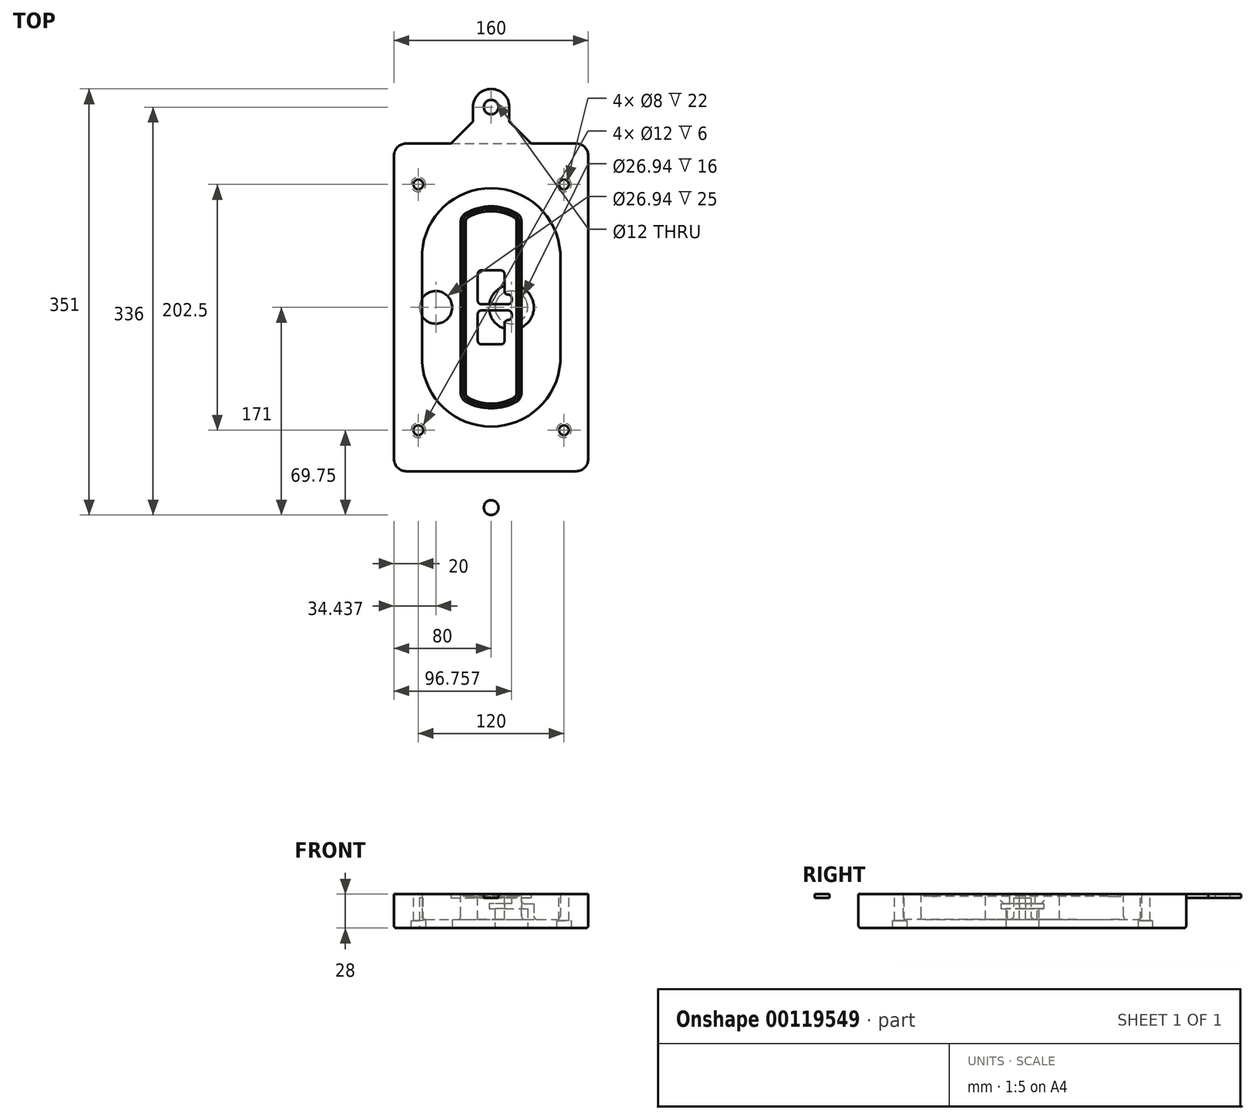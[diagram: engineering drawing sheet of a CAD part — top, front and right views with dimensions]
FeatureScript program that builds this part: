
annotation { "Feature Type Name" : "Feature", "Feature Type Description" : "" }
export const myFeature = defineFeature(function(context is Context, id is Id, definition is map)
    precondition{}
    {
        {
            var Q0;
            Q0=qCreatedBy(makeId("Top.planeOp"),FACE);
            var sketch = newSketch(context, id + "F0", { "sketchPlane" : qUnion([Q0])});
            skPoint(sketch, "E0.rect.middle", {"position": v(0, 0) * mm});
            skLineSegment(sketch, "E1.bottom", {"start": v(-70, -135) * mm, "end": v(70, -135) * mm});
            skLineSegment(sketch, "E1.top", {"start": v(-70, 135) * mm, "end": v(70, 135) * mm});
            skLineSegment(sketch, "E1.left", {"start": v(-80, -125) * mm, "end": v(-80, 125) * mm});
            skLineSegment(sketch, "E1.right", {"start": v(80, -125) * mm, "end": v(80, 125) * mm});
            skLineSegment(sketch, "E2", {"start": v(-80, 135) * mm, "end": v(80, -135) * mm, "construction": true});
            skLineSegment(sketch, "E3", {"start": v(80, 135) * mm, "end": v(-80, -135) * mm, "construction": true});
            skCircle(sketch, "E4", {"center": v(-60, 101.25) * mm, "radius": 4 * mm});
            skCircle(sketch, "E5", {"center": v(60, 101.25) * mm, "radius": 4 * mm});
            skCircle(sketch, "E6", {"center": v(60, -101.25) * mm, "radius": 4 * mm});
            skCircle(sketch, "E7", {"center": v(-60, -101.25) * mm, "radius": 4 * mm});
            skLineSegment(sketch, "E8", {"start": v(-60, 101.25) * mm, "end": v(60, 101.25) * mm, "construction": true});
            skLineSegment(sketch, "E9", {"start": v(60, 101.25) * mm, "end": v(60, -101.25) * mm, "construction": true});
            skLineSegment(sketch, "E10", {"start": v(60, -101.25) * mm, "end": v(-60, -101.25) * mm, "construction": true});
            skLineSegment(sketch, "E11", {"start": v(-60, -101.25) * mm, "end": v(-60, 101.25) * mm, "construction": true});
            skLineSegment(sketch, "E12", {"start": v(-60, 44.66) * mm, "end": v(-60, -44.66) * mm});
            skLineSegment(sketch, "E13", {"start": v(60, 44.66) * mm, "end": v(60, -44.66) * mm});
            skArc(sketch, "E14", {"start": v(59.98, 45.37) * mm, "mid": v(0, 101.25) * mm, "end": v(-59.98, 45.37) * mm});
            skArc(sketch, "E15", {"start": v(-59.98, -45.37) * mm, "mid": v(0, -101.25) * mm, "end": v(59.98, -45.37) * mm});
            skLineSegment(sketch, "E16", {"start": v(-60, 0) * mm, "end": v(60, 0) * mm, "construction": true});
            skPoint(sketch, "E17.visualSharp", {"position": v(-60, -45) * mm});
            skArc(sketch, "E17.filletArc", {"start": v(-60, -44.66) * mm, "mid": v(-60, -45.02) * mm, "end": v(-59.98, -45.37) * mm});
            skPoint(sketch, "E18.visualSharp", {"position": v(-60, 45) * mm});
            skArc(sketch, "E18.filletArc", {"start": v(-59.98, 45.37) * mm, "mid": v(-60, 45.02) * mm, "end": v(-60, 44.66) * mm});
            skPoint(sketch, "E19.visualSharp", {"position": v(60, 45) * mm});
            skArc(sketch, "E19.filletArc", {"start": v(60, 44.66) * mm, "mid": v(60, 45.02) * mm, "end": v(59.98, 45.37) * mm});
            skPoint(sketch, "E20.visualSharp", {"position": v(60, -45) * mm});
            skArc(sketch, "E20.filletArc", {"start": v(59.98, -45.37) * mm, "mid": v(60, -45.02) * mm, "end": v(60, -44.66) * mm});
            skPoint(sketch, "E21.visualSharp", {"position": v(-80, 135) * mm});
            skArc(sketch, "E21.filletArc", {"start": v(-70, 135) * mm, "mid": v(-77.07, 132.07) * mm, "end": v(-80, 125) * mm});
            skPoint(sketch, "E22.visualSharp", {"position": v(80, 135) * mm});
            skArc(sketch, "E22.filletArc", {"start": v(80, 125) * mm, "mid": v(77.07, 132.07) * mm, "end": v(70, 135) * mm});
            skPoint(sketch, "E23.visualSharp", {"position": v(80, -135) * mm});
            skArc(sketch, "E23.filletArc", {"start": v(70, -135) * mm, "mid": v(77.07, -132.07) * mm, "end": v(80, -125) * mm});
            skPoint(sketch, "E24.visualSharp", {"position": v(-80, -135) * mm});
            skArc(sketch, "E24.filletArc", {"start": v(-80, -125) * mm, "mid": v(-77.07, -132.07) * mm, "end": v(-70, -135) * mm});
            skArc(sketch, "E25.0", {"start": v(57, 44.66) * mm, "mid": v(57, 44.9) * mm, "end": v(56.98, 45.16) * mm});
            skLineSegment(sketch, "E25.1", {"start": v(57, 44.66) * mm, "end": v(57, -44.66) * mm});
            skArc(sketch, "E25.2", {"start": v(56.98, -45.16) * mm, "mid": v(57, -44.9) * mm, "end": v(57, -44.66) * mm});
            skArc(sketch, "E25.3", {"start": v(-56.98, -45.16) * mm, "mid": v(0, -98.25) * mm, "end": v(56.98, -45.16) * mm});
            skArc(sketch, "E25.4", {"start": v(-57, -44.66) * mm, "mid": v(-57, -44.9) * mm, "end": v(-56.98, -45.16) * mm});
            skArc(sketch, "E25.5", {"start": v(56.98, 45.16) * mm, "mid": v(0, 98.25) * mm, "end": v(-56.98, 45.16) * mm});
            skLineSegment(sketch, "E25.6", {"start": v(-57, 44.66) * mm, "end": v(-57, -44.66) * mm});
            skArc(sketch, "E25.7", {"start": v(-56.98, 45.16) * mm, "mid": v(-57, 44.9) * mm, "end": v(-57, 44.66) * mm});
            skArc(sketch, "E26.0", {"start": v(-63.97, 45.65) * mm, "mid": v(-64, 45.16) * mm, "end": v(-64, 44.66) * mm});
            skArc(sketch, "E26.1", {"start": v(63.97, 45.65) * mm, "mid": v(0, 105.25) * mm, "end": v(-63.97, 45.65) * mm});
            skArc(sketch, "E26.2", {"start": v(64, 44.66) * mm, "mid": v(64, 45.16) * mm, "end": v(63.97, 45.65) * mm});
            skLineSegment(sketch, "E26.3", {"start": v(64, 44.66) * mm, "end": v(64, -44.66) * mm});
            skArc(sketch, "E26.4", {"start": v(63.97, -45.65) * mm, "mid": v(64, -45.16) * mm, "end": v(64, -44.66) * mm});
            skLineSegment(sketch, "E26.5", {"start": v(-64, 44.66) * mm, "end": v(-64, -44.66) * mm});
            skArc(sketch, "E26.6", {"start": v(-63.97, -45.65) * mm, "mid": v(0, -105.25) * mm, "end": v(63.97, -45.65) * mm});
            skArc(sketch, "E26.7", {"start": v(-64, -44.66) * mm, "mid": v(-64, -45.16) * mm, "end": v(-63.97, -45.65) * mm});
            skSolve(sketch);
        }
        {
            var Q0;
            Q0=makeQuery(id+"F0.imprint","IMPRINT",FACE,{"disambiguationData":[TD([[makeQuery(id+"F0.imprint","IMPRINT",EDGE,{"derivedFrom":sQuery(id+"F0.wireOp",EDGE,"E1.bottom")}),1.0]])]});
            var Q1;
            Q1=makeQuery(id+"F0.imprint","IMPRINT",FACE,{"disambiguationData":[TD([[makeQuery(id+"F0.imprint","IMPRINT",EDGE,{"derivedFrom":sQuery(id+"F0.wireOp",EDGE,"E12")}),1.0]])]});
            var Q2;
            Q2=makeQuery(id+"F0.imprint","IMPRINT",FACE,{"disambiguationData":[TD([[makeQuery(id+"F0.imprint","IMPRINT",EDGE,{"derivedFrom":sQuery(id+"F0.wireOp",EDGE,"E25.0")}),1.0]])]});
            var Q3;
            Q3=makeQuery(id+"F0.imprint","IMPRINT",FACE,{"disambiguationData":[TD([[makeQuery(id+"F0.imprint","IMPRINT",EDGE,{"derivedFrom":sQuery(id+"F0.wireOp",EDGE,"E12")}),-1.0]])]});
            extrude(context, id + "F1", {"entities" : qUnion([Q0, Q1, Q2, Q3]), "oppositeDirection" : true, "depth" : 25 * mm});
        }
        {
            var Q0;
            Q0=makeQuery(id+"F0.imprint","IMPRINT",FACE,{"disambiguationData":[TD([[makeQuery(id+"F0.imprint","IMPRINT",EDGE,{"derivedFrom":sQuery(id+"F0.wireOp",EDGE,"E12")}),1.0]])]});
            extrude(context, id + "F2", {"entities" : qUnion([Q0]), "operationType" : NewBodyOperationType.ADD, "depth" : 3 * mm});
        }
        {
            var Q0;
            Q0=makeQuery(id+"F0.imprint","IMPRINT",FACE,{"disambiguationData":[TD([[makeQuery(id+"F0.imprint","IMPRINT",EDGE,{"derivedFrom":sQuery(id+"F0.wireOp",EDGE,"E25.0")}),1.0]])]});
            extrude(context, id + "F3", {"entities" : qUnion([Q0]), "operationType" : NewBodyOperationType.REMOVE, "oppositeDirection" : true, "depth" : 18 * mm});
        }
        {
            var Q0;
            Q0=makeQuery(id+"F2.opExtrude","CAP_FACE",FACE,{"disambiguationData":[OSD([sQuery(id+"F0.wireOp",EDGE,"E12"),sQuery(id+"F0.wireOp",EDGE,"E13"),sQuery(id+"F0.wireOp",EDGE,"E14"),sQuery(id+"F0.wireOp",EDGE,"E15"),sQuery(id+"F0.wireOp",EDGE,"E17.filletArc"),sQuery(id+"F0.wireOp",EDGE,"E18.filletArc"),sQuery(id+"F0.wireOp",EDGE,"E19.filletArc"),sQuery(id+"F0.wireOp",EDGE,"E20.filletArc"),sQuery(id+"F0.wireOp",EDGE,"E25.0"),sQuery(id+"F0.wireOp",EDGE,"E25.1"),sQuery(id+"F0.wireOp",EDGE,"E25.2"),sQuery(id+"F0.wireOp",EDGE,"E25.3"),sQuery(id+"F0.wireOp",EDGE,"E25.4"),sQuery(id+"F0.wireOp",EDGE,"E25.5"),sQuery(id+"F0.wireOp",EDGE,"E25.6"),sQuery(id+"F0.wireOp",EDGE,"E25.7")])],"isStart":false});
            var sketch = newSketch(context, id + "F4", { "sketchPlane" : qUnion([Q0])});
            skArc(sketch, "E27.0", {"start": v(-20.99, -77.65) * mm, "mid": v(0, -83.25) * mm, "end": v(20.99, -77.65) * mm});
            skArc(sketch, "E28.0", {"start": v(20.99, 77.65) * mm, "mid": v(0, 83.25) * mm, "end": v(-20.99, 77.65) * mm});
            skLineSegment(sketch, "E29", {"start": v(-25, 70.71) * mm, "end": v(-25, -70.71) * mm});
            skLineSegment(sketch, "E30", {"start": v(25, 70.71) * mm, "end": v(25, -70.71) * mm});
            skLineSegment(sketch, "E31", {"start": v(-25, 75.03) * mm, "end": v(25, 75.03) * mm, "construction": true});
            skLineSegment(sketch, "E32", {"start": v(-25, -75.03) * mm, "end": v(25, -75.03) * mm, "construction": true});
            skPoint(sketch, "E33.visualSharp", {"position": v(-25, 75.03) * mm});
            skArc(sketch, "E33.filletArc", {"start": v(-20.99, 77.65) * mm, "mid": v(-23.92, 74.72) * mm, "end": v(-25, 70.71) * mm});
            skPoint(sketch, "E34.visualSharp", {"position": v(25, 75.03) * mm});
            skArc(sketch, "E34.filletArc", {"start": v(25, 70.71) * mm, "mid": v(23.92, 74.72) * mm, "end": v(20.99, 77.65) * mm});
            skPoint(sketch, "E35.visualSharp", {"position": v(25, -75.03) * mm});
            skArc(sketch, "E35.filletArc", {"start": v(20.99, -77.65) * mm, "mid": v(23.92, -74.72) * mm, "end": v(25, -70.71) * mm});
            skPoint(sketch, "E36.visualSharp", {"position": v(-25, -75.03) * mm});
            skArc(sketch, "E36.filletArc", {"start": v(-25, -70.71) * mm, "mid": v(-23.92, -74.72) * mm, "end": v(-20.99, -77.65) * mm});
            skArc(sketch, "E37.0", {"start": v(56.98, 45.16) * mm, "mid": v(0, 98.25) * mm, "end": v(-56.98, 45.16) * mm});
            skArc(sketch, "E37.1", {"start": v(-56.98, 45.16) * mm, "mid": v(-57, 44.9) * mm, "end": v(-57, 44.66) * mm});
            skLineSegment(sketch, "E37.2", {"start": v(-57, 44.66) * mm, "end": v(-57, -44.66) * mm});
            skArc(sketch, "E37.3", {"start": v(-57, -44.66) * mm, "mid": v(-57, -44.9) * mm, "end": v(-56.98, -45.16) * mm});
            skArc(sketch, "E37.4", {"start": v(-56.98, -45.16) * mm, "mid": v(0, -98.25) * mm, "end": v(56.98, -45.16) * mm});
            skArc(sketch, "E37.5", {"start": v(56.98, -45.16) * mm, "mid": v(57, -44.9) * mm, "end": v(57, -44.66) * mm});
            skLineSegment(sketch, "E37.6", {"start": v(57, 44.66) * mm, "end": v(57, -44.66) * mm});
            skArc(sketch, "E37.7", {"start": v(57, 44.66) * mm, "mid": v(57, 44.9) * mm, "end": v(56.98, 45.16) * mm});
            skLineSegment(sketch, "E38.0", {"start": v(23, 70.71) * mm, "end": v(23, -70.71) * mm});
            skArc(sketch, "E38.1", {"start": v(19.99, -75.92) * mm, "mid": v(22.2, -73.72) * mm, "end": v(23, -70.71) * mm});
            skArc(sketch, "E38.2", {"start": v(-19.99, -75.92) * mm, "mid": v(0, -81.25) * mm, "end": v(19.99, -75.92) * mm});
            skArc(sketch, "E38.3", {"start": v(-23, -70.71) * mm, "mid": v(-22.2, -73.72) * mm, "end": v(-19.99, -75.92) * mm});
            skLineSegment(sketch, "E38.4", {"start": v(-23, 70.71) * mm, "end": v(-23, -70.71) * mm});
            skArc(sketch, "E38.5", {"start": v(23, 70.71) * mm, "mid": v(22.2, 73.72) * mm, "end": v(19.99, 75.92) * mm});
            skArc(sketch, "E38.6", {"start": v(-19.99, 75.92) * mm, "mid": v(-22.2, 73.72) * mm, "end": v(-23, 70.71) * mm});
            skArc(sketch, "E38.7", {"start": v(19.99, 75.92) * mm, "mid": v(0, 81.25) * mm, "end": v(-19.99, 75.92) * mm});
            skArc(sketch, "E39.0", {"start": v(21, 70.71) * mm, "mid": v(20.46, 72.72) * mm, "end": v(19, 74.18) * mm});
            skLineSegment(sketch, "E39.1", {"start": v(21, 70.71) * mm, "end": v(21, -70.71) * mm});
            skArc(sketch, "E39.2", {"start": v(19, -74.18) * mm, "mid": v(20.46, -72.72) * mm, "end": v(21, -70.71) * mm});
            skArc(sketch, "E39.3", {"start": v(-19, -74.18) * mm, "mid": v(0, -79.25) * mm, "end": v(19, -74.18) * mm});
            skArc(sketch, "E39.4", {"start": v(-21, -70.71) * mm, "mid": v(-20.46, -72.72) * mm, "end": v(-19, -74.18) * mm});
            skArc(sketch, "E39.5", {"start": v(19, 74.18) * mm, "mid": v(0, 79.25) * mm, "end": v(-19, 74.18) * mm});
            skLineSegment(sketch, "E39.6", {"start": v(-21, 70.71) * mm, "end": v(-21, -70.71) * mm});
            skArc(sketch, "E39.7", {"start": v(-19, 74.18) * mm, "mid": v(-20.46, 72.72) * mm, "end": v(-21, 70.71) * mm});
            skLineSegment(sketch, "E40", {"start": v(-25, 0) * mm, "end": v(25, 0) * mm, "construction": true});
            skLineSegment(sketch, "E41", {"start": v(-11, 5.5) * mm, "end": v(-11, 27.5) * mm});
            skLineSegment(sketch, "E42", {"start": v(-8, 30.5) * mm, "end": v(8, 30.5) * mm});
            skLineSegment(sketch, "E43", {"start": v(11, 27.5) * mm, "end": v(11, 13.5) * mm});
            skLineSegment(sketch, "E44", {"start": v(14, 10.5) * mm, "end": v(14, 10.5) * mm});
            skLineSegment(sketch, "E45", {"start": v(17, 7.5) * mm, "end": v(17, 5.5) * mm});
            skLineSegment(sketch, "E46", {"start": v(14, 2.5) * mm, "end": v(-8, 2.5) * mm});
            skPoint(sketch, "E47.visualSharp", {"position": v(-11, 30.5) * mm});
            skArc(sketch, "E47.filletArc", {"start": v(-8, 30.5) * mm, "mid": v(-10.12, 29.62) * mm, "end": v(-11, 27.5) * mm});
            skPoint(sketch, "E48.visualSharp", {"position": v(11, 30.5) * mm});
            skArc(sketch, "E48.filletArc", {"start": v(11, 27.5) * mm, "mid": v(10.12, 29.62) * mm, "end": v(8, 30.5) * mm});
            skPoint(sketch, "E49.visualSharp", {"position": v(11, 10.5) * mm});
            skArc(sketch, "E49.filletArc", {"start": v(11, 13.5) * mm, "mid": v(11.88, 11.38) * mm, "end": v(14, 10.5) * mm});
            skPoint(sketch, "E50.visualSharp", {"position": v(17, 10.5) * mm});
            skArc(sketch, "E50.filletArc", {"start": v(17, 7.5) * mm, "mid": v(16.12, 9.62) * mm, "end": v(14, 10.5) * mm});
            skPoint(sketch, "E51.visualSharp", {"position": v(17, 2.5) * mm});
            skArc(sketch, "E51.filletArc", {"start": v(14, 2.5) * mm, "mid": v(16.12, 3.38) * mm, "end": v(17, 5.5) * mm});
            skPoint(sketch, "E52.visualSharp", {"position": v(-11, 2.5) * mm});
            skArc(sketch, "E52.filletArc", {"start": v(-11, 5.5) * mm, "mid": v(-10.12, 3.38) * mm, "end": v(-8, 2.5) * mm});
            skLineSegment(sketch, "E53.0.MirrorCS", {"start": v(14, -2.5) * mm, "end": v(-8, -2.5) * mm});
            skArc(sketch, "E54.0.MirrorCS", {"start": v(-11, -5.5) * mm, "mid": v(-10.12, -3.38) * mm, "end": v(-8, -2.5) * mm});
            skLineSegment(sketch, "E55.0.MirrorCS", {"start": v(-11, -5.5) * mm, "end": v(-11, -27.5) * mm});
            skArc(sketch, "E56.0.MirrorCS", {"start": v(-8, -30.5) * mm, "mid": v(-10.12, -29.62) * mm, "end": v(-11, -27.5) * mm});
            skLineSegment(sketch, "E57.0.MirrorCS", {"start": v(-8, -30.5) * mm, "end": v(8, -30.5) * mm});
            skArc(sketch, "E58.0.MirrorCS", {"start": v(11, -27.5) * mm, "mid": v(10.12, -29.62) * mm, "end": v(8, -30.5) * mm});
            skLineSegment(sketch, "E59.0.MirrorCS", {"start": v(11, -27.5) * mm, "end": v(11, -13.5) * mm});
            skArc(sketch, "E60.0.MirrorCS", {"start": v(11, -13.5) * mm, "mid": v(11.88, -11.38) * mm, "end": v(14, -10.5) * mm});
            skArc(sketch, "E61.0.MirrorCS", {"start": v(17, -7.5) * mm, "mid": v(16.12, -9.62) * mm, "end": v(14, -10.5) * mm});
            skLineSegment(sketch, "E62.0.MirrorCS", {"start": v(17, -7.5) * mm, "end": v(17, -5.5) * mm});
            skArc(sketch, "E63.0.MirrorCS", {"start": v(14, -2.5) * mm, "mid": v(16.12, -3.38) * mm, "end": v(17, -5.5) * mm});
            skSolve(sketch);
        }
        {
            var Q0;
            Q0=makeQuery(id+"F4.imprint","IMPRINT",FACE,{"disambiguationData":[TD([[makeQuery(id+"F4.imprint","IMPRINT",EDGE,{"derivedFrom":sQuery(id+"F4.wireOp",EDGE,"E27.0")}),1.0]])]});
            var Q1;
            Q1=makeQuery(id+"F4.imprint","IMPRINT",FACE,{"disambiguationData":[TD([[makeQuery(id+"F4.imprint","IMPRINT",EDGE,{"derivedFrom":sQuery(id+"F4.wireOp",EDGE,"E38.0")}),-1.0]])]});
            var Q2;
            Q2=makeQuery(id+"F4.imprint","IMPRINT",FACE,{"disambiguationData":[TD([[makeQuery(id+"F4.imprint","IMPRINT",EDGE,{"derivedFrom":sQuery(id+"F4.wireOp",EDGE,"E39.0")}),1.0]])]});
            extrude(context, id + "F5", {"entities" : qUnion([Q0, Q1, Q2]), "operationType" : NewBodyOperationType.ADD, "endBound" : BoundingType.UP_TO_NEXT, "oppositeDirection" : true, "depth" : 25 * mm});
        }
        {
            var Q0;
            Q0=makeQuery(id+"F4.imprint","IMPRINT",FACE,{"disambiguationData":[TD([[makeQuery(id+"F4.imprint","IMPRINT",EDGE,{"derivedFrom":sQuery(id+"F4.wireOp",EDGE,"E38.0")}),-1.0]])]});
            extrude(context, id + "F6", {"entities" : qUnion([Q0]), "operationType" : NewBodyOperationType.REMOVE, "oppositeDirection" : true, "depth" : 2 * mm});
        }
        {
            var Q0;
            Q0=makeQuery(id+"F1.opExtrude","CAP_FACE",FACE,{"disambiguationData":[OSD([sQuery(id+"F0.wireOp",EDGE,"E1.bottom"),sQuery(id+"F0.wireOp",EDGE,"E1.top"),sQuery(id+"F0.wireOp",EDGE,"E1.left"),sQuery(id+"F0.wireOp",EDGE,"E1.right"),sQuery(id+"F0.wireOp",EDGE,"E4"),sQuery(id+"F0.wireOp",EDGE,"E5"),sQuery(id+"F0.wireOp",EDGE,"E6"),sQuery(id+"F0.wireOp",EDGE,"E7"),sQuery(id+"F0.wireOp",EDGE,"E21.filletArc"),sQuery(id+"F0.wireOp",EDGE,"E22.filletArc"),sQuery(id+"F0.wireOp",EDGE,"E23.filletArc"),sQuery(id+"F0.wireOp",EDGE,"E24.filletArc")])],"isStart":false});
            var sketch = newSketch(context, id + "F7", { "sketchPlane" : qUnion([Q0])});
            skCircle(sketch, "E64", {"center": v(16.76, 0) * mm, "radius": 13.47 * mm});
            skCircle(sketch, "E65", {"center": v(-45.56, 0) * mm, "radius": 13.47 * mm});
            skLineSegment(sketch, "E66", {"start": v(80, 0) * mm, "end": v(-80, 0) * mm});
            skCircle(sketch, "E67", {"center": v(16.76, 0) * mm, "radius": 18.47 * mm});
            skCircle(sketch, "E68", {"center": v(60, -101.25) * mm, "radius": 6 * mm});
            skCircle(sketch, "E69", {"center": v(-60, -101.25) * mm, "radius": 6 * mm});
            skCircle(sketch, "E70", {"center": v(-60, 101.25) * mm, "radius": 6 * mm});
            skCircle(sketch, "E71", {"center": v(60, 101.25) * mm, "radius": 6 * mm});
            skSolve(sketch);
        }
        {
            var Q0;
            {var subQ1=sQuery(id+"F7.wireOp",EDGE,"E66");var subQ4=sQuery(id+"F7.wireOp",EDGE,"E64");var subQ6=makeQuery(id+"F7.imprint","INTERSECT",VERTEX,{"disambiguationData":[OD(0.0)],"derivedFrom":[subQ4,subQ1]});Q0=makeQuery(id+"F7.imprint","IMPRINT",FACE,{"disambiguationData":[TD([[makeQuery(id+"F7.imprint","IMPRINT",EDGE,{"disambiguationData":[TD([[subQ6,-1.0]])],"derivedFrom":subQ4}),-1.0]])]});}
            var Q1;
            {var subQ0=sQuery(id+"F7.wireOp",EDGE,"E66");var subQ1=sQuery(id+"F7.wireOp",EDGE,"E64");var subQ3=makeQuery(id+"F7.imprint","INTERSECT",VERTEX,{"disambiguationData":[OD(0.0)],"derivedFrom":[subQ1,subQ0]});Q1=makeQuery(id+"F7.imprint","IMPRINT",FACE,{"disambiguationData":[TD([[makeQuery(id+"F7.imprint","IMPRINT",EDGE,{"disambiguationData":[TD([[subQ3,-1.0]])],"derivedFrom":subQ1}),1.0]])]});}
            var Q2;
            {var subQ0=sQuery(id+"F7.wireOp",EDGE,"E66");var subQ1=sQuery(id+"F7.wireOp",EDGE,"E64");var subQ3=makeQuery(id+"F7.imprint","INTERSECT",VERTEX,{"disambiguationData":[OD(0.0)],"derivedFrom":[subQ1,subQ0]});Q2=makeQuery(id+"F7.imprint","IMPRINT",FACE,{"disambiguationData":[TD([[makeQuery(id+"F7.imprint","IMPRINT",EDGE,{"disambiguationData":[TD([[subQ3,1.0]])],"derivedFrom":subQ1}),1.0]])]});}
            var Q3;
            {var subQ1=sQuery(id+"F7.wireOp",EDGE,"E66");var subQ4=sQuery(id+"F7.wireOp",EDGE,"E64");var subQ6=makeQuery(id+"F7.imprint","INTERSECT",VERTEX,{"disambiguationData":[OD(0.0)],"derivedFrom":[subQ4,subQ1]});Q3=makeQuery(id+"F7.imprint","IMPRINT",FACE,{"disambiguationData":[TD([[makeQuery(id+"F7.imprint","IMPRINT",EDGE,{"disambiguationData":[TD([[subQ6,1.0]])],"derivedFrom":subQ4}),-1.0]])]});}
            extrude(context, id + "F8", {"entities" : qUnion([Q0, Q1, Q2, Q3]), "operationType" : NewBodyOperationType.ADD, "oppositeDirection" : true, "depth" : 20 * mm});
        }
        {
            var Q0;
            {var subQ0=sQuery(id+"F7.wireOp",EDGE,"E66");var subQ1=sQuery(id+"F7.wireOp",EDGE,"E64");var subQ3=makeQuery(id+"F7.imprint","INTERSECT",VERTEX,{"disambiguationData":[OD(0.0)],"derivedFrom":[subQ1,subQ0]});Q0=makeQuery(id+"F7.imprint","IMPRINT",FACE,{"disambiguationData":[TD([[makeQuery(id+"F7.imprint","IMPRINT",EDGE,{"disambiguationData":[TD([[subQ3,-1.0]])],"derivedFrom":subQ1}),1.0]])]});}
            var Q1;
            {var subQ0=sQuery(id+"F7.wireOp",EDGE,"E66");var subQ1=sQuery(id+"F7.wireOp",EDGE,"E64");var subQ3=makeQuery(id+"F7.imprint","INTERSECT",VERTEX,{"disambiguationData":[OD(0.0)],"derivedFrom":[subQ1,subQ0]});Q1=makeQuery(id+"F7.imprint","IMPRINT",FACE,{"disambiguationData":[TD([[makeQuery(id+"F7.imprint","IMPRINT",EDGE,{"disambiguationData":[TD([[subQ3,1.0]])],"derivedFrom":subQ1}),1.0]])]});}
            extrude(context, id + "F9", {"entities" : qUnion([Q0, Q1]), "operationType" : NewBodyOperationType.REMOVE, "oppositeDirection" : true, "depth" : 16 * mm});
        }
        {
            var Q0;
            {var subQ0=sQuery(id+"F7.wireOp",EDGE,"E66");var subQ1=sQuery(id+"F7.wireOp",EDGE,"E65");var subQ3=makeQuery(id+"F7.imprint","INTERSECT",VERTEX,{"disambiguationData":[OD(0.0)],"derivedFrom":[subQ1,subQ0]});Q0=makeQuery(id+"F7.imprint","IMPRINT",FACE,{"disambiguationData":[TD([[makeQuery(id+"F7.imprint","IMPRINT",EDGE,{"disambiguationData":[TD([[subQ3,-1.0]])],"derivedFrom":subQ1}),1.0]])]});}
            var Q1;
            {var subQ0=sQuery(id+"F7.wireOp",EDGE,"E66");var subQ1=sQuery(id+"F7.wireOp",EDGE,"E65");var subQ3=makeQuery(id+"F7.imprint","INTERSECT",VERTEX,{"disambiguationData":[OD(0.0)],"derivedFrom":[subQ1,subQ0]});Q1=makeQuery(id+"F7.imprint","IMPRINT",FACE,{"disambiguationData":[TD([[makeQuery(id+"F7.imprint","IMPRINT",EDGE,{"disambiguationData":[TD([[subQ3,1.0]])],"derivedFrom":subQ1}),1.0]])]});}
            extrude(context, id + "F10", {"entities" : qUnion([Q0, Q1]), "operationType" : NewBodyOperationType.REMOVE, "oppositeDirection" : true, "depth" : 25 * mm});
        }
        {
            var Q0;
            Q0=makeQuery(id+"F7.imprint","IMPRINT",FACE,{"disambiguationData":[TD([[makeQuery(id+"F7.imprint","IMPRINT",EDGE,{"derivedFrom":sQuery(id+"F7.wireOp",EDGE,"E68")}),1.0]])]});
            var Q1;
            Q1=makeQuery(id+"F7.imprint","IMPRINT",FACE,{"disambiguationData":[TD([[makeQuery(id+"F7.imprint","IMPRINT",EDGE,{"derivedFrom":makeQuery(id+"F1.opExtrude","CAP_EDGE",EDGE,{"disambiguationData":[OSD([sQuery(id+"F0.wireOp",EDGE,"E5")])],"isStart":false})}),-1.0]])]});
            var Q2;
            Q2=makeQuery(id+"F7.imprint","IMPRINT",FACE,{"disambiguationData":[TD([[makeQuery(id+"F7.imprint","IMPRINT",EDGE,{"derivedFrom":sQuery(id+"F7.wireOp",EDGE,"E69")}),1.0]])]});
            var Q3;
            Q3=makeQuery(id+"F7.imprint","IMPRINT",FACE,{"disambiguationData":[TD([[makeQuery(id+"F7.imprint","IMPRINT",EDGE,{"derivedFrom":makeQuery(id+"F1.opExtrude","CAP_EDGE",EDGE,{"disambiguationData":[OSD([sQuery(id+"F0.wireOp",EDGE,"E4")])],"isStart":false})}),-1.0]])]});
            var Q4;
            Q4=makeQuery(id+"F7.imprint","IMPRINT",FACE,{"disambiguationData":[TD([[makeQuery(id+"F7.imprint","IMPRINT",EDGE,{"derivedFrom":sQuery(id+"F7.wireOp",EDGE,"E70")}),1.0]])]});
            var Q5;
            Q5=makeQuery(id+"F7.imprint","IMPRINT",FACE,{"disambiguationData":[TD([[makeQuery(id+"F7.imprint","IMPRINT",EDGE,{"derivedFrom":makeQuery(id+"F1.opExtrude","CAP_EDGE",EDGE,{"disambiguationData":[OSD([sQuery(id+"F0.wireOp",EDGE,"E7")])],"isStart":false})}),-1.0]])]});
            var Q6;
            Q6=makeQuery(id+"F7.imprint","IMPRINT",FACE,{"disambiguationData":[TD([[makeQuery(id+"F7.imprint","IMPRINT",EDGE,{"derivedFrom":sQuery(id+"F7.wireOp",EDGE,"E71")}),1.0]])]});
            var Q7;
            Q7=makeQuery(id+"F7.imprint","IMPRINT",FACE,{"disambiguationData":[TD([[makeQuery(id+"F7.imprint","IMPRINT",EDGE,{"derivedFrom":makeQuery(id+"F1.opExtrude","CAP_EDGE",EDGE,{"disambiguationData":[OSD([sQuery(id+"F0.wireOp",EDGE,"E6")])],"isStart":false})}),-1.0]])]});
            extrude(context, id + "F11", {"entities" : qUnion([Q0, Q1, Q2, Q3, Q4, Q5, Q6, Q7]), "operationType" : NewBodyOperationType.REMOVE, "oppositeDirection" : true, "depth" : 6 * mm});
        }
        {
            var Q0;
            Q0=makeQuery(id+"F9.boolean.opBoolean","COPY",FACE,{"derivedFrom":makeQuery(id+"F9.opExtrude","CAP_FACE",FACE,{"disambiguationData":[OSD([sQuery(id+"F7.wireOp",EDGE,"E64")])],"isStart":false})});
            var sketch = newSketch(context, id + "F12", { "sketchPlane" : qUnion([Q0])});
            skArc(sketch, "E72.0", {"start": v(11, 17.55) * mm, "mid": v(2.57, 11.82) * mm, "end": v(-1.54, 2.5) * mm});
            skArc(sketch, "E72.1", {"start": v(-1.54, -2.5) * mm, "mid": v(2.57, -11.82) * mm, "end": v(11, -17.55) * mm});
            skLineSegment(sketch, "E73", {"start": v(-1.54, -2.5) * mm, "end": v(14, -2.5) * mm});
            skLineSegment(sketch, "E74.0", {"start": v(14, 2.5) * mm, "end": v(-1.54, 2.5) * mm});
            skArc(sketch, "E74.1", {"start": v(14, 2.5) * mm, "mid": v(16.12, 3.38) * mm, "end": v(17, 5.5) * mm});
            skLineSegment(sketch, "E74.2", {"start": v(17, 7.5) * mm, "end": v(17, 5.5) * mm});
            skArc(sketch, "E74.3", {"start": v(17, 7.5) * mm, "mid": v(16.12, 9.62) * mm, "end": v(14, 10.5) * mm});
            skArc(sketch, "E74.4", {"start": v(11, 13.5) * mm, "mid": v(11.88, 11.38) * mm, "end": v(14, 10.5) * mm});
            skLineSegment(sketch, "E74.5", {"start": v(11, 17.55) * mm, "end": v(11, 13.5) * mm});
            skLineSegment(sketch, "E74.7", {"start": v(14, -2.5) * mm, "end": v(-1.54, -2.5) * mm});
            skArc(sketch, "E74.8", {"start": v(14, -2.5) * mm, "mid": v(16.12, -3.38) * mm, "end": v(17, -5.5) * mm});
            skLineSegment(sketch, "E74.9", {"start": v(17, -7.5) * mm, "end": v(17, -5.5) * mm});
            skArc(sketch, "E74.10", {"start": v(17, -7.5) * mm, "mid": v(16.12, -9.62) * mm, "end": v(14, -10.5) * mm});
            skArc(sketch, "E74.11", {"start": v(11, -13.5) * mm, "mid": v(11.88, -11.38) * mm, "end": v(14, -10.5) * mm});
            skLineSegment(sketch, "E74.12", {"start": v(11, -17.55) * mm, "end": v(11, -13.5) * mm});
            skPoint(sketch, "E75.orphan", {"position": v(11, -27.5) * mm});
            skPoint(sketch, "E76.orphan", {"position": v(-8, -2.5) * mm});
            skPoint(sketch, "E77.orphan", {"position": v(-8, 2.5) * mm});
            skPoint(sketch, "E78.orphan", {"position": v(11, 27.5) * mm});
            skSolve(sketch);
        }
        {
            var Q0;
            {var subQ7=sQuery(id+"F12.wireOp",EDGE,"E72.0");var subQ14=sQuery(id+"F12.wireOp",EDGE,"E72.1");var subQ16=sQuery(id+"F12.wireOp",EDGE,"E74.1");var subQ18=sQuery(id+"F12.wireOp",EDGE,"E74.8");Q0=qUnion([makeQuery(id+"F12.imprint","IMPRINT",FACE,{"disambiguationData":[TD([[makeQuery(id+"F12.imprint","IMPRINT",EDGE,{"derivedFrom":subQ7}),1.0]])]}),makeQuery(id+"F12.imprint","IMPRINT",FACE,{"disambiguationData":[TD([[makeQuery(id+"F12.imprint","IMPRINT",EDGE,{"derivedFrom":subQ14}),1.0]])]}),makeQuery(id+"F12.imprint","IMPRINT",FACE,{"disambiguationData":[TD([[makeQuery(id+"F12.imprint","IMPRINT",EDGE,{"derivedFrom":subQ16}),1.0]])]}),makeQuery(id+"F12.imprint","IMPRINT",FACE,{"disambiguationData":[TD([[makeQuery(id+"F12.imprint","IMPRINT",EDGE,{"derivedFrom":subQ18}),-1.0]])]})]);}
            var Q1;
            Q1=makeQuery(id+"F5.boolean.opBoolean","SPLIT",FACE,{"disambiguationData":[TD([makeQuery(id+"F5.opExtrude","SWEPT_FACE",FACE,{"disambiguationData":[OSD([sQuery(id+"F4.wireOp",EDGE,"E41")])]})])],"derivedFrom":makeQuery(id+"F3.boolean.opBoolean","COPY",FACE,{"derivedFrom":makeQuery(id+"F3.opExtrude","CAP_FACE",FACE,{"disambiguationData":[OSD([sQuery(id+"F0.wireOp",EDGE,"E25.0"),sQuery(id+"F0.wireOp",EDGE,"E25.1"),sQuery(id+"F0.wireOp",EDGE,"E25.2"),sQuery(id+"F0.wireOp",EDGE,"E25.3"),sQuery(id+"F0.wireOp",EDGE,"E25.4"),sQuery(id+"F0.wireOp",EDGE,"E25.5"),sQuery(id+"F0.wireOp",EDGE,"E25.6"),sQuery(id+"F0.wireOp",EDGE,"E25.7")])],"isStart":false})})});
            extrude(context, id + "F13", {"entities" : qUnion([Q0]), "operationType" : NewBodyOperationType.REMOVE, "endBound" : BoundingType.UP_TO_SURFACE, "endBoundEntityFace" : qUnion([Q1]), "depth" : 25 * mm});
        }
        {
            var Q0;
            Q0=makeQuery(id+"F3.boolean.opBoolean","COPY",EDGE,{"derivedFrom":makeQuery(id+"F3.opExtrude","CAP_EDGE",EDGE,{"disambiguationData":[OSD([sQuery(id+"F0.wireOp",EDGE,"E25.6")])],"isStart":false})});
            var Q1;
            Q1=makeQuery(id+"F8.boolean.opBoolean","INTERSECT",EDGE,{"derivedFrom":[makeQuery(id+"F5.opExtrude","SWEPT_FACE",FACE,{"disambiguationData":[OSD([sQuery(id+"F4.wireOp",EDGE,"E30")])]}),makeQuery(id+"F8.opExtrude","CAP_FACE",FACE,{"disambiguationData":[OSD([sQuery(id+"F7.wireOp",EDGE,"E67")])],"isStart":false})]});
            var Q2;
            Q2=makeQuery(id+"F8.boolean.opBoolean","INTERSECT",EDGE,{"disambiguationData":[OD(1.0)],"derivedFrom":[makeQuery(id+"F5.opExtrude","SWEPT_FACE",FACE,{"disambiguationData":[OSD([sQuery(id+"F4.wireOp",EDGE,"E30")])]}),makeQuery(id+"F8.opExtrude","SWEPT_FACE",FACE,{"disambiguationData":[OSD([sQuery(id+"F7.wireOp",EDGE,"E67")])]})]});
            var Q3;
            {var subQ0=sQuery(id+"F4.wireOp",EDGE,"E30");Q3=makeQuery(id+"F8.boolean.opBoolean","SPLIT",EDGE,{"disambiguationData":[TD([makeQuery(id+"F5.opExtrude","SWEPT_FACE",FACE,{"disambiguationData":[OSD([sQuery(id+"F4.wireOp",EDGE,"E35.filletArc")])]})])],"derivedFrom":makeQuery(id+"F5.opExtrude","CAP_EDGE",EDGE,{"disambiguationData":[OSD([subQ0])],"isStart":false})});}
            var Q4;
            {var subQ0=sQuery(id+"F0.wireOp",EDGE,"E25.7");var subQ1=sQuery(id+"F0.wireOp",EDGE,"E25.1");var subQ2=sQuery(id+"F0.wireOp",EDGE,"E25.6");var subQ3=sQuery(id+"F0.wireOp",EDGE,"E25.5");var subQ4=sQuery(id+"F0.wireOp",EDGE,"E25.4");var subQ5=sQuery(id+"F0.wireOp",EDGE,"E25.0");var subQ6=sQuery(id+"F0.wireOp",EDGE,"E25.2");var subQ7=sQuery(id+"F0.wireOp",EDGE,"E25.3");Q4=makeQuery(id+"F8.boolean.opBoolean","INTERSECT",EDGE,{"derivedFrom":[makeQuery(id+"F5.boolean.opBoolean","SPLIT",FACE,{"disambiguationData":[TD([makeQuery(id+"F2.opExtrude","SWEPT_FACE",FACE,{"disambiguationData":[OSD([subQ5])]})])],"derivedFrom":makeQuery(id+"F3.boolean.opBoolean","COPY",FACE,{"derivedFrom":makeQuery(id+"F3.opExtrude","CAP_FACE",FACE,{"disambiguationData":[OSD([subQ5,subQ1,subQ6,subQ7,subQ4,subQ3,subQ2,subQ0])],"isStart":false})})}),makeQuery(id+"F8.opExtrude","SWEPT_FACE",FACE,{"disambiguationData":[OSD([sQuery(id+"F7.wireOp",EDGE,"E67")])]})]});}
            var Q5;
            Q5=makeQuery(id+"F8.boolean.opBoolean","INTERSECT",EDGE,{"disambiguationData":[OD(0.0)],"derivedFrom":[makeQuery(id+"F5.opExtrude","SWEPT_FACE",FACE,{"disambiguationData":[OSD([sQuery(id+"F4.wireOp",EDGE,"E30")])]}),makeQuery(id+"F8.opExtrude","SWEPT_FACE",FACE,{"disambiguationData":[OSD([sQuery(id+"F7.wireOp",EDGE,"E67")])]})]});
            fillet(context, id + "F14", {"entities" : qUnion([Q0, Q1, Q2, Q3, Q4, Q5]), "radius" : 3 * mm, "tangentPropagation" : true, "allowEdgeOverflow" : false});
        }
        {
            var Q0;
            Q0=makeQuery(id+"F1.opExtrude","CAP_EDGE",EDGE,{"disambiguationData":[OSD([sQuery(id+"F0.wireOp",EDGE,"E1.bottom")])],"isStart":false});
            fillet(context, id + "F15", {"entities" : qUnion([Q0]), "radius" : 2 * mm, "tangentPropagation" : true, "allowEdgeOverflow" : false});
        }
        {
            var Q0;
            {var subQ0=sQuery(id+"F0.wireOp",EDGE,"E22.filletArc");var subQ1=sQuery(id+"F0.wireOp",EDGE,"E7");var subQ2=sQuery(id+"F0.wireOp",EDGE,"E6");var subQ3=sQuery(id+"F0.wireOp",EDGE,"E5");var subQ4=sQuery(id+"F0.wireOp",EDGE,"E4");var subQ5=sQuery(id+"F0.wireOp",EDGE,"E1.bottom");var subQ6=sQuery(id+"F0.wireOp",EDGE,"E21.filletArc");var subQ7=sQuery(id+"F0.wireOp",EDGE,"E1.top");var subQ8=sQuery(id+"F0.wireOp",EDGE,"E1.left");var subQ9=sQuery(id+"F0.wireOp",EDGE,"E1.right");var subQ10=sQuery(id+"F0.wireOp",EDGE,"E23.filletArc");var subQ11=sQuery(id+"F0.wireOp",EDGE,"E24.filletArc");Q0=makeQuery(id+"F2.boolean.opBoolean","SPLIT",FACE,{"disambiguationData":[TD([makeQuery(id+"F1.opExtrude","SWEPT_FACE",FACE,{"disambiguationData":[OSD([subQ5])]})])],"derivedFrom":makeQuery(id+"F1.opExtrude","CAP_FACE",FACE,{"disambiguationData":[OSD([subQ5,subQ7,subQ8,subQ9,subQ4,subQ3,subQ2,subQ1,subQ6,subQ0,subQ10,subQ11])],"isStart":true})});}
            var sketch = newSketch(context, id + "F16", { "sketchPlane" : qUnion([Q0])});
            skCircle(sketch, "E79", {"center": v(0, 165) * mm, "radius": 6 * mm});
            skLineSegment(sketch, "E80", {"start": v(0, 165) * mm, "end": v(0, 135) * mm, "construction": true});
            skLineSegment(sketch, "E81", {"start": v(-33, 135) * mm, "end": v(-15, 153) * mm});
            skLineSegment(sketch, "E82", {"start": v(33, 135) * mm, "end": v(15, 153) * mm});
            skLineSegment(sketch, "E83", {"start": v(-15, 153) * mm, "end": v(-15, 165) * mm});
            skLineSegment(sketch, "E84", {"start": v(15, 153) * mm, "end": v(15, 165) * mm});
            skArc(sketch, "E85", {"start": v(15, 165) * mm, "mid": v(0, 180) * mm, "end": v(-15, 165) * mm});
            skLineSegment(sketch, "E86", {"start": v(-80, 0) * mm, "end": v(80, 0) * mm, "construction": true});
            skCircle(sketch, "E87.MirrorC", {"center": v(0, -165) * mm, "radius": 6 * mm});
            skArc(sketch, "E88.MirrorCS", {"start": v(15, -165) * mm, "mid": v(0, -180) * mm, "end": v(-15, -165) * mm});
            skLineSegment(sketch, "E89.MirrorCS", {"start": v(15, -153) * mm, "end": v(15, -165) * mm});
            skLineSegment(sketch, "E90.MirrorCS", {"start": v(-15, -153) * mm, "end": v(-15, -165) * mm});
            skLineSegment(sketch, "E91.MirrorCS", {"start": v(0, -165) * mm, "end": v(0, -135) * mm, "construction": true});
            skLineSegment(sketch, "E92.MirrorCS", {"start": v(33, -135) * mm, "end": v(15, -153) * mm});
            skLineSegment(sketch, "E93.MirrorCS", {"start": v(-33, -135) * mm, "end": v(-15, -153) * mm});
            skSolve(sketch);
        }
        {
            var Q0;
            Q0=makeQuery(id+"F16.imprint","IMPRINT",FACE,{"disambiguationData":[TD([[makeQuery(id+"F16.imprint","IMPRINT",EDGE,{"derivedFrom":sQuery(id+"F16.wireOp",EDGE,"E79")}),-1.0]])]});
            var Q1;
            Q1=makeQuery(id+"F16.imprint","IMPRINT",FACE,{"disambiguationData":[TD([[makeQuery(id+"F16.imprint","IMPRINT",EDGE,{"derivedFrom":sQuery(id+"F16.wireOp",EDGE,"E87.MirrorC")}),1.0]])]});
            var Q2;
            Q2=makeQuery(id+"F16.imprint","IMPRINT",FACE,{"disambiguationData":[TD([[makeQuery(id+"F16.imprint","IMPRINT",EDGE,{"derivedFrom":makeQuery(id+"F1.opExtrude","CAP_EDGE",EDGE,{"disambiguationData":[OSD([sQuery(id+"F0.wireOp",EDGE,"E1.left")])],"isStart":true})}),-1.0]])]});
            var Q3;
            Q3=makeQuery(id+"F2.opExtrude","CAP_FACE",FACE,{"disambiguationData":[OSD([sQuery(id+"F0.wireOp",EDGE,"E12"),sQuery(id+"F0.wireOp",EDGE,"E13"),sQuery(id+"F0.wireOp",EDGE,"E14"),sQuery(id+"F0.wireOp",EDGE,"E15"),sQuery(id+"F0.wireOp",EDGE,"E17.filletArc"),sQuery(id+"F0.wireOp",EDGE,"E18.filletArc"),sQuery(id+"F0.wireOp",EDGE,"E19.filletArc"),sQuery(id+"F0.wireOp",EDGE,"E20.filletArc"),sQuery(id+"F0.wireOp",EDGE,"E25.0"),sQuery(id+"F0.wireOp",EDGE,"E25.1"),sQuery(id+"F0.wireOp",EDGE,"E25.2"),sQuery(id+"F0.wireOp",EDGE,"E25.3"),sQuery(id+"F0.wireOp",EDGE,"E25.4"),sQuery(id+"F0.wireOp",EDGE,"E25.5"),sQuery(id+"F0.wireOp",EDGE,"E25.6"),sQuery(id+"F0.wireOp",EDGE,"E25.7")])],"isStart":false});
            extrude(context, id + "F17", {"entities" : qUnion([Q0, Q1, Q2]), "operationType" : NewBodyOperationType.ADD, "endBound" : BoundingType.UP_TO_SURFACE, "endBoundEntityFace" : qUnion([Q3]), "depth" : 25 * mm});
        }
    });
